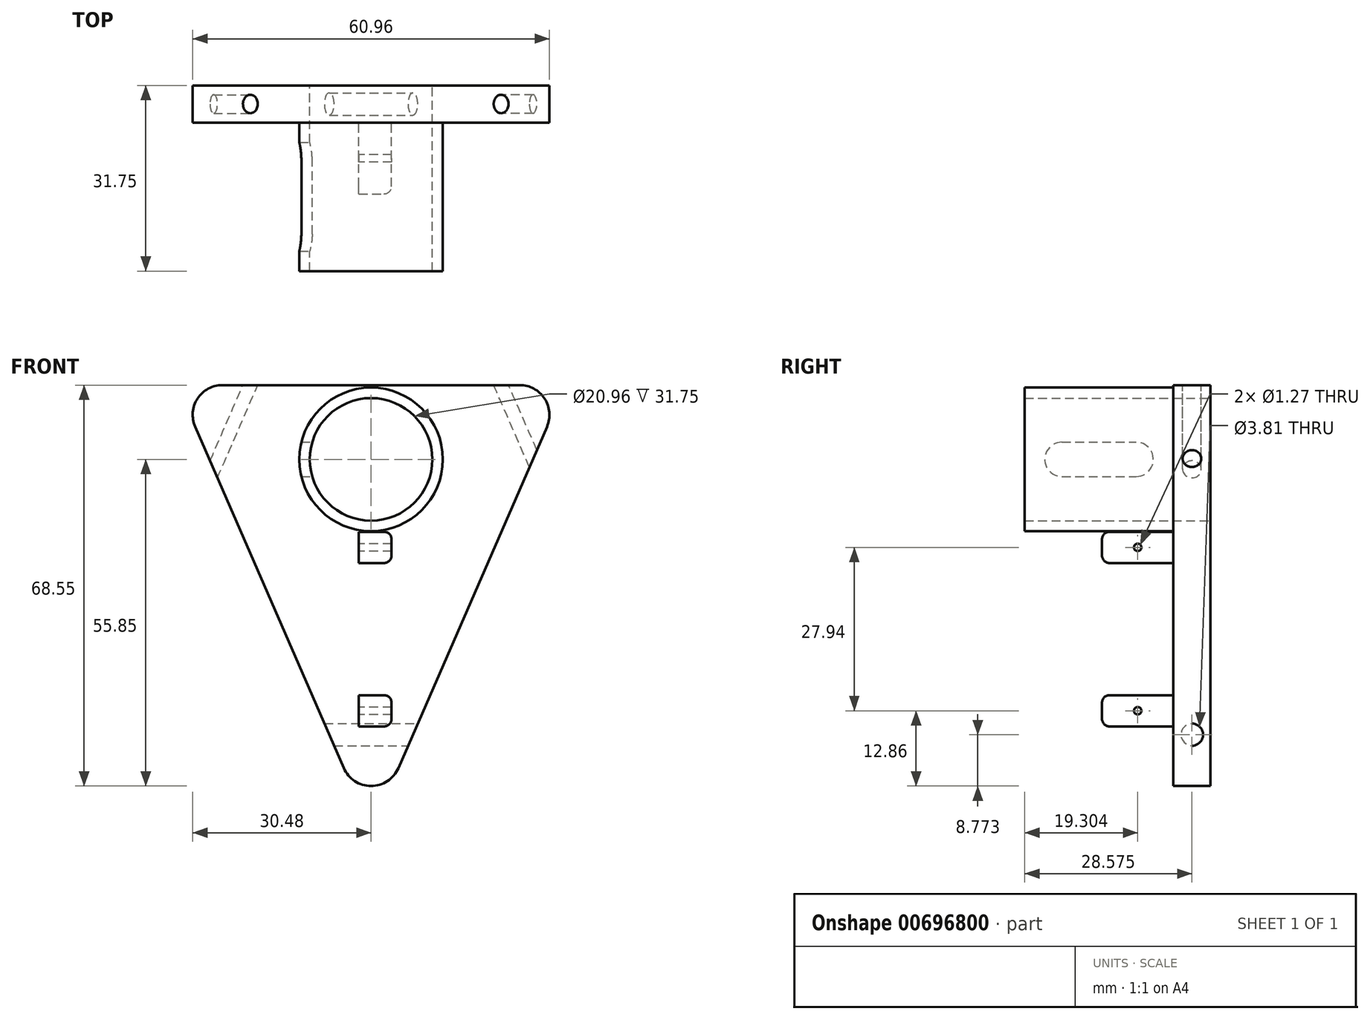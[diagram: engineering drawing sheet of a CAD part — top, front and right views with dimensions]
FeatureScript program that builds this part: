
annotation { "Feature Type Name" : "Feature", "Feature Type Description" : "" }
export const myFeature = defineFeature(function(context is Context, id is Id, definition is map)
    precondition{}
    {
        {
            var Q0;
            Q0=qCreatedBy(makeId("Front.planeOp"),FACE);
            var sketch = newSketch(context, id + "F0", { "sketchPlane" : qUnion([Q0])});
            skLineSegment(sketch, "E0", {"start": v(4.66, -27.4) * mm, "end": v(30.06, 31) * mm});
            skLineSegment(sketch, "E1", {"start": v(25.4, 38.1) * mm, "end": v(0, 38.1) * mm});
            skLineSegment(sketch, "E2", {"start": v(0, 38.1) * mm, "end": v(-25.4, 38.1) * mm});
            skLineSegment(sketch, "E3", {"start": v(-30.06, 31) * mm, "end": v(-4.66, -27.4) * mm});
            skPoint(sketch, "E4.visualSharp", {"position": v(-33.15, 38.1) * mm});
            skArc(sketch, "E4.filletArc", {"start": v(-25.4, 38.1) * mm, "mid": v(-29.65, 35.8) * mm, "end": v(-30.06, 31) * mm});
            skPoint(sketch, "E5.visualSharp", {"position": v(0, -38.1) * mm});
            skArc(sketch, "E5.filletArc", {"start": v(-4.66, -27.4) * mm, "mid": v(0, -30.45) * mm, "end": v(4.66, -27.4) * mm});
            skPoint(sketch, "E6.visualSharp", {"position": v(33.15, 38.1) * mm});
            skArc(sketch, "E6.filletArc", {"start": v(30.06, 31) * mm, "mid": v(29.65, 35.8) * mm, "end": v(25.4, 38.1) * mm});
            skCircle(sketch, "E7", {"center": v(0, 25.4) * mm, "radius": 10.48 * mm});
            skSolve(sketch);
        }
        {
            var Q0;
            Q0=makeQuery(id+"F0.imprint","IMPRINT",FACE,{"disambiguationData":[TD([[makeQuery(id+"F0.imprint","IMPRINT",EDGE,{"derivedFrom":sQuery(id+"F0.wireOp",EDGE,"E0")}),1.0]])]});
            extrude(context, id + "F1", {"entities" : qUnion([Q0]), "depth" : 6.35 * mm, "offsetDistance" : 25.4 * mm});
        }
        {
            var Q0;
            Q0=qCreatedBy(makeId("Right.planeOp"),FACE);
            var sketch = newSketch(context, id + "F2", { "sketchPlane" : qUnion([Q0])});
            skCircle(sketch, "E8", {"center": v(-3.18, -21.68) * mm, "radius": 1.9 * mm});
            skSolve(sketch);
        }
        {
            var Q0;
            Q0 = qSketchRegion(id + "F2", true);
            extrude(context, id + "F3", {"entities" : qUnion([Q0]), "operationType" : NewBodyOperationType.REMOVE, "endBound" : BoundingType.SYMMETRIC, "oppositeDirection" : true, "depth" : 18.14 * mm, "offsetDistance" : 25.4 * mm});
        }
        {
            var Q0;
            Q0=makeQuery(id+"F1.opExtrude","CAP_FACE",FACE,{"disambiguationData":[OSD([sQuery(id+"F0.wireOp",EDGE,"E0"),sQuery(id+"F0.wireOp",EDGE,"E1"),sQuery(id+"F0.wireOp",EDGE,"E2"),sQuery(id+"F0.wireOp",EDGE,"E3"),sQuery(id+"F0.wireOp",EDGE,"E4.filletArc"),sQuery(id+"F0.wireOp",EDGE,"E5.filletArc"),sQuery(id+"F0.wireOp",EDGE,"E6.filletArc"),sQuery(id+"F0.wireOp",EDGE,"E7")])],"isStart":false});
            var sketch = newSketch(context, id + "F4", { "sketchPlane" : qUnion([Q0])});
            skLineSegment(sketch, "E9.bottom", {"start": v(-2.1, 13.02) * mm, "end": v(2.22, 13.02) * mm});
            skLineSegment(sketch, "E9.top", {"start": v(-2.1, 7.68) * mm, "end": v(2.22, 7.68) * mm});
            skLineSegment(sketch, "E9.left", {"start": v(-2.1, 13.02) * mm, "end": v(-2.1, 7.68) * mm});
            skLineSegment(sketch, "E9.right", {"start": v(3.5, 11.75) * mm, "end": v(3.5, 8.95) * mm});
            skPoint(sketch, "E10.visualSharp", {"position": v(3.5, 7.68) * mm});
            skArc(sketch, "E10.filletArc", {"start": v(2.22, 7.68) * mm, "mid": v(3.12, 8.06) * mm, "end": v(3.5, 8.95) * mm});
            skPoint(sketch, "E11.visualSharp", {"position": v(3.5, 13.02) * mm});
            skArc(sketch, "E11.filletArc", {"start": v(3.5, 11.75) * mm, "mid": v(3.12, 12.65) * mm, "end": v(2.22, 13.02) * mm});
            skLineSegment(sketch, "E12.bottom", {"start": v(-2.1, -14.92) * mm, "end": v(2.22, -14.92) * mm});
            skLineSegment(sketch, "E12.top", {"start": v(-2.1, -20.26) * mm, "end": v(2.22, -20.26) * mm});
            skLineSegment(sketch, "E12.left", {"start": v(-2.1, -14.92) * mm, "end": v(-2.1, -20.26) * mm});
            skLineSegment(sketch, "E12.right", {"start": v(3.5, -16.2) * mm, "end": v(3.5, -18.99) * mm});
            skPoint(sketch, "E13.visualSharp", {"position": v(3.5, -20.26) * mm});
            skArc(sketch, "E13.filletArc", {"start": v(2.22, -20.26) * mm, "mid": v(3.12, -19.88) * mm, "end": v(3.5, -18.99) * mm});
            skPoint(sketch, "E14.visualSharp", {"position": v(3.5, -14.92) * mm});
            skArc(sketch, "E14.filletArc", {"start": v(3.5, -16.2) * mm, "mid": v(3.12, -15.3) * mm, "end": v(2.22, -14.92) * mm});
            skSolve(sketch);
        }
        {
            var Q0;
            Q0 = qSketchRegion(id + "F4", true);
            extrude(context, id + "F5", {"entities" : qUnion([Q0]), "operationType" : NewBodyOperationType.ADD, "depth" : 12.2 * mm, "offsetDistance" : 25.4 * mm});
        }
        {
            var Q0;
            Q0=makeQuery(id+"F5.opExtrude","SWEPT_FACE",FACE,{"disambiguationData":[OSD([sQuery(id+"F4.wireOp",EDGE,"E12.left")])]});
            var sketch = newSketch(context, id + "F6", { "sketchPlane" : qUnion([Q0])});
            skCircle(sketch, "E15", {"center": v(12.45, -17.59) * mm, "radius": 0.64 * mm});
            skPoint(sketch, "E15.centerSnap0", {"position": v(12.45, -14.92) * mm});
            skPoint(sketch, "E15.centerSnap1", {"position": v(18.54, -17.59) * mm});
            skSolve(sketch);
        }
        {
            var Q0;
            Q0=makeQuery(id+"F5.opExtrude","SWEPT_FACE",FACE,{"disambiguationData":[OSD([sQuery(id+"F4.wireOp",EDGE,"E9.left")])]});
            var sketch = newSketch(context, id + "F7", { "sketchPlane" : qUnion([Q0])});
            skCircle(sketch, "E16", {"center": v(12.45, 10.35) * mm, "radius": 0.64 * mm});
            skPoint(sketch, "E16.centerSnap0", {"position": v(12.45, 7.68) * mm});
            skPoint(sketch, "E16.centerSnap1", {"position": v(18.54, 10.35) * mm});
            skSolve(sketch);
        }
        {
            var Q0;
            Q0=makeQuery(id+"F6.imprint","IMPRINT",FACE,{"disambiguationData":[TD([[makeQuery(id+"F6.imprint","IMPRINT",EDGE,{"derivedFrom":sQuery(id+"F6.wireOp",EDGE,"E15")}),1.0]])]});
            var Q1;
            Q1=makeQuery(id+"F7.imprint","IMPRINT",FACE,{"disambiguationData":[TD([[makeQuery(id+"F7.imprint","IMPRINT",EDGE,{"derivedFrom":sQuery(id+"F7.wireOp",EDGE,"E16")}),1.0]])]});
            extrude(context, id + "F8", {"entities" : qUnion([Q0, Q1]), "operationType" : NewBodyOperationType.REMOVE, "endBound" : BoundingType.THROUGH_ALL, "oppositeDirection" : true, "depth" : 25.4 * mm, "offsetDistance" : 25.4 * mm});
        }
        {
            var Q0;
            Q0=makeQuery(id+"F5.opExtrude","CAP_EDGE",EDGE,{"disambiguationData":[OSD([sQuery(id+"F4.wireOp",EDGE,"E9.bottom")])],"isStart":false});
            var Q1;
            Q1=makeQuery(id+"F5.opExtrude","CAP_EDGE",EDGE,{"disambiguationData":[OSD([sQuery(id+"F4.wireOp",EDGE,"E11.filletArc")])],"isStart":false});
            var Q2;
            Q2=makeQuery(id+"F5.opExtrude","CAP_EDGE",EDGE,{"disambiguationData":[OSD([sQuery(id+"F4.wireOp",EDGE,"E9.right")])],"isStart":false});
            var Q3;
            Q3=makeQuery(id+"F5.opExtrude","CAP_EDGE",EDGE,{"disambiguationData":[OSD([sQuery(id+"F4.wireOp",EDGE,"E10.filletArc")])],"isStart":false});
            var Q4;
            Q4=makeQuery(id+"F5.opExtrude","CAP_EDGE",EDGE,{"disambiguationData":[OSD([sQuery(id+"F4.wireOp",EDGE,"E9.top")])],"isStart":false});
            var Q5;
            Q5=makeQuery(id+"F5.opExtrude","CAP_EDGE",EDGE,{"disambiguationData":[OSD([sQuery(id+"F4.wireOp",EDGE,"E12.top")])],"isStart":false});
            var Q6;
            Q6=makeQuery(id+"F5.opExtrude","CAP_EDGE",EDGE,{"disambiguationData":[OSD([sQuery(id+"F4.wireOp",EDGE,"E12.right")])],"isStart":false});
            var Q7;
            Q7=makeQuery(id+"F5.opExtrude","CAP_EDGE",EDGE,{"disambiguationData":[OSD([sQuery(id+"F4.wireOp",EDGE,"E14.filletArc")])],"isStart":false});
            var Q8;
            Q8=makeQuery(id+"F5.opExtrude","CAP_EDGE",EDGE,{"disambiguationData":[OSD([sQuery(id+"F4.wireOp",EDGE,"E12.bottom")])],"isStart":false});
            fillet(context, id + "F9", {"entities" : qUnion([Q0, Q1, Q2, Q3, Q4, Q5, Q6, Q7, Q8]), "radius" : 1.27 * mm, "tangentPropagation" : true, "allowEdgeOverflow" : false});
        }
        {
            var Q0;
            Q0=makeQuery(id+"F1.opExtrude","CAP_FACE",FACE,{"disambiguationData":[OSD([sQuery(id+"F0.wireOp",EDGE,"E0"),sQuery(id+"F0.wireOp",EDGE,"E1"),sQuery(id+"F0.wireOp",EDGE,"E2"),sQuery(id+"F0.wireOp",EDGE,"E3"),sQuery(id+"F0.wireOp",EDGE,"E4.filletArc"),sQuery(id+"F0.wireOp",EDGE,"E5.filletArc"),sQuery(id+"F0.wireOp",EDGE,"E6.filletArc"),sQuery(id+"F0.wireOp",EDGE,"E7")])],"isStart":false});
            var sketch = newSketch(context, id + "F10", { "sketchPlane" : qUnion([Q0])});
            skCircle(sketch, "E17", {"center": v(0, 25.4) * mm, "radius": 12.27 * mm});
            skSolve(sketch);
        }
        {
            var Q0;
            Q0=makeQuery(id+"F10.imprint","IMPRINT",FACE,{"disambiguationData":[TD([[makeQuery(id+"F10.imprint","IMPRINT",EDGE,{"derivedFrom":sQuery(id+"F10.wireOp",EDGE,"E17")}),1.0]])]});
            extrude(context, id + "F11", {"entities" : qUnion([Q0]), "operationType" : NewBodyOperationType.ADD, "depth" : 25.4 * mm, "offsetDistance" : 25.4 * mm});
        }
        {
            var Q0;
            Q0=qCreatedBy(makeId("Right.planeOp"),FACE);
            var sketch = newSketch(context, id + "F12", { "sketchPlane" : qUnion([Q0])});
            skArc(sketch, "E18", {"start": v(-12.7, 22.47) * mm, "mid": v(-9.77, 25.4) * mm, "end": v(-12.7, 28.33) * mm});
            skArc(sketch, "E19", {"start": v(-25.4, 28.33) * mm, "mid": v(-28.33, 25.4) * mm, "end": v(-25.4, 22.47) * mm});
            skLineSegment(sketch, "E20", {"start": v(-12.7, 28.33) * mm, "end": v(-25.4, 28.33) * mm});
            skLineSegment(sketch, "E21", {"start": v(-12.7, 22.47) * mm, "end": v(-25.4, 22.47) * mm});
            skSolve(sketch);
        }
        {
            var Q0;
            Q0 = qSketchRegion(id + "F12", true);
            extrude(context, id + "F13", {"entities" : qUnion([Q0]), "operationType" : NewBodyOperationType.REMOVE, "oppositeDirection" : true, "depth" : 12.7 * mm, "offsetDistance" : 25.4 * mm});
        }
        {
            var Q0;
            Q0=makeQuery(id+"F1.opExtrude","SWEPT_FACE",FACE,{"disambiguationData":[OSD([sQuery(id+"F0.wireOp",EDGE,"E3")])]});
            var sketch = newSketch(context, id + "F14", { "sketchPlane" : qUnion([Q0])});
            skCircle(sketch, "E22", {"center": v(3.18, 32.46) * mm, "radius": 1.59 * mm});
            skPoint(sketch, "E22.centerSnap0", {"position": v(3.18, 40.41) * mm});
            skSolve(sketch);
        }
        {
            var Q0;
            Q0=makeQuery(id+"F14.imprint","IMPRINT",FACE,{"disambiguationData":[TD([[makeQuery(id+"F14.imprint","IMPRINT",EDGE,{"derivedFrom":sQuery(id+"F14.wireOp",EDGE,"E22")}),1.0]])]});
            var Q1;
            Q1=sQuery(id+"F14.wireOp",EDGE,"E22");
            var Q2;
            Q2=makeQuery(id+"F1.opExtrude","CAP_EDGE",EDGE,{"disambiguationData":[OSD([sQuery(id+"F0.wireOp",EDGE,"E0")])],"isStart":false});
            sweep(context, id + "F15", {"operationType" : NewBodyOperationType.REMOVE, "profiles" : qUnion([Q0]), "surfaceProfiles" : qUnion([Q1]), "path" : qUnion([Q2])});
        }
        {
            var Q0;
            Q0=makeQuery(id+"F1.opExtrude","SWEPT_FACE",FACE,{"disambiguationData":[OSD([sQuery(id+"F0.wireOp",EDGE,"E0")])]});
            var sketch = newSketch(context, id + "F16", { "sketchPlane" : qUnion([Q0])});
            skCircle(sketch, "E23", {"center": v(-3.18, 34.46) * mm, "radius": 1.59 * mm});
            skPoint(sketch, "E23.centerSnap0", {"position": v(-3.18, 40.41) * mm});
            skSolve(sketch);
        }
        {
            var Q0;
            Q0=makeQuery(id+"F16.imprint","IMPRINT",FACE,{"disambiguationData":[TD([[makeQuery(id+"F16.imprint","IMPRINT",EDGE,{"derivedFrom":sQuery(id+"F16.wireOp",EDGE,"E23")}),1.0]])]});
            var Q1;
            Q1=makeQuery(id+"F1.opExtrude","CAP_EDGE",EDGE,{"disambiguationData":[OSD([sQuery(id+"F0.wireOp",EDGE,"E3")])],"isStart":false});
            sweep(context, id + "F17", {"operationType" : NewBodyOperationType.REMOVE, "profiles" : qUnion([Q0]), "path" : qUnion([Q1])});
        }
    });
